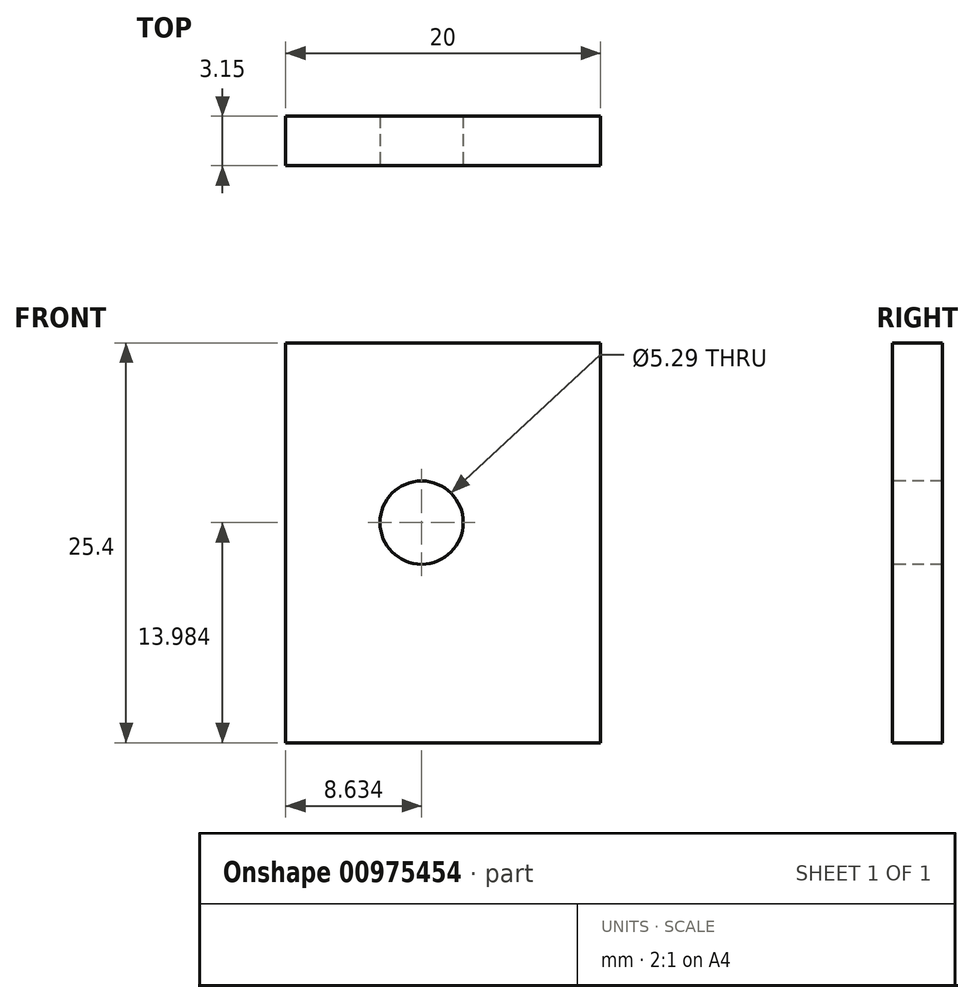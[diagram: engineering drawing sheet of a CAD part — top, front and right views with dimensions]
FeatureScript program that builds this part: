
annotation { "Feature Type Name" : "Feature", "Feature Type Description" : "" }
export const myFeature = defineFeature(function(context is Context, id is Id, definition is map)
    precondition{}
    {
        {
            var Q0;
            Q0=qCreatedBy(makeId("Top.planeOp"),FACE);
            var sketch = newSketch(context, id + "F0", { "sketchPlane" : qUnion([Q0])});
            skLineSegment(sketch, "E0", {"start": v(-11.3, 0.65) * mm, "end": v(8.7, 0.65) * mm});
            skLineSegment(sketch, "E1", {"start": v(8.7, 0.65) * mm, "end": v(8.7, -2.5) * mm});
            skLineSegment(sketch, "E2", {"start": v(8.7, -2.5) * mm, "end": v(-11.3, -2.5) * mm});
            skLineSegment(sketch, "E3", {"start": v(-11.3, -2.5) * mm, "end": v(-11.3, 0.65) * mm});
            skSolve(sketch);
        }
        {
            var Q0;
            Q0 = qSketchRegion(id + "F0", true);
            extrude(context, id + "F1", {"entities" : qUnion([Q0]), "depth" : 25.4 * mm, "offsetDistance" : 25.4 * mm});
        }
        {
            var Q0;
            Q0=makeQuery(id+"F1.opExtrude","SWEPT_FACE",FACE,{"disambiguationData":[OSD([sQuery(id+"F0.wireOp",EDGE,"E2")])]});
            var sketch = newSketch(context, id + "F2", { "sketchPlane" : qUnion([Q0])});
            skCircle(sketch, "E4", {"center": v(-2.66, 13.98) * mm, "radius": 2.64 * mm});
            skSolve(sketch);
        }
        {
            var Q0;
            Q0 = qSketchRegion(id + "F2", true);
            extrude(context, id + "F3", {"entities" : qUnion([Q0]), "operationType" : NewBodyOperationType.REMOVE, "oppositeDirection" : true, "depth" : 25.4 * mm, "offsetDistance" : 25.4 * mm});
        }
    });
